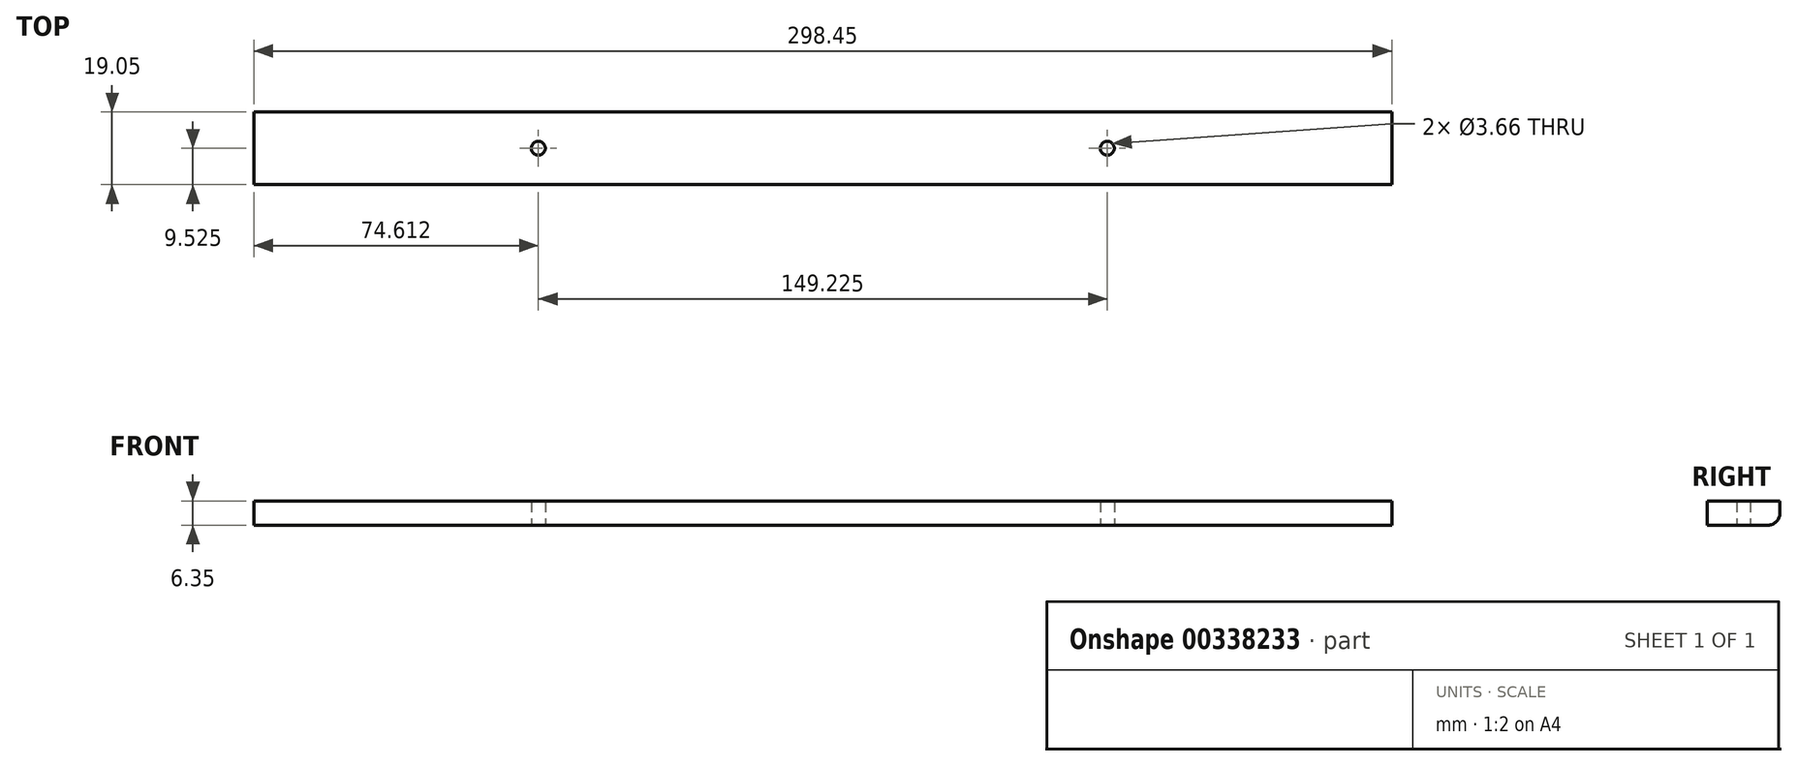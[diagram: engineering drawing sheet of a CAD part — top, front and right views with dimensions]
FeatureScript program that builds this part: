
annotation { "Feature Type Name" : "Feature", "Feature Type Description" : "" }
export const myFeature = defineFeature(function(context is Context, id is Id, definition is map)
    precondition{}
    {
        {
            var Q0;
            Q0=qCreatedBy(makeId("Top.planeOp"),FACE);
            var sketch = newSketch(context, id + "F0", { "sketchPlane" : qUnion([Q0])});
            skLineSegment(sketch, "E0.bottom", {"start": v(0, 0) * mm, "end": v(298.45, 0) * mm});
            skLineSegment(sketch, "E0.top", {"start": v(0, -19.05) * mm, "end": v(298.45, -19.05) * mm});
            skLineSegment(sketch, "E0.left", {"start": v(0, 0) * mm, "end": v(0, -19.05) * mm});
            skLineSegment(sketch, "E0.right", {"start": v(298.45, 0) * mm, "end": v(298.45, -19.05) * mm});
            skLineSegment(sketch, "E1", {"start": v(298.45, -9.53) * mm, "end": v(223.84, -9.53) * mm, "construction": true});
            skPoint(sketch, "E1.endSnap0", {"position": v(298.45, -9.53) * mm});
            skLineSegment(sketch, "E2", {"start": v(223.84, -9.53) * mm, "end": v(149.23, -9.53) * mm, "construction": true});
            skLineSegment(sketch, "E3", {"start": v(149.23, -9.53) * mm, "end": v(74.61, -9.53) * mm, "construction": true});
            skLineSegment(sketch, "E4", {"start": v(74.61, -9.53) * mm, "end": v(0, -9.53) * mm, "construction": true});
            skCircle(sketch, "E5", {"center": v(74.61, -9.53) * mm, "radius": 1.83 * mm});
            skCircle(sketch, "E6", {"center": v(223.84, -9.53) * mm, "radius": 1.83 * mm});
            skSolve(sketch);
        }
        {
            var Q0;
            Q0 = qSketchRegion(id + "F0", true);
            extrude(context, id + "F1", {"entities" : qUnion([Q0]), "depth" : 6.35 * mm});
        }
        {
            var Q0;
            Q0=makeQuery(id+"F1.opExtrude","CAP_EDGE",EDGE,{"disambiguationData":[OSD([sQuery(id+"F0.wireOp",EDGE,"E0.bottom")])],"isStart":true});
            fillet(context, id + "F2", {"entities" : qUnion([Q0]), "radius" : 3.17 * mm, "tangentPropagation" : true, "allowEdgeOverflow" : false});
        }
    });
